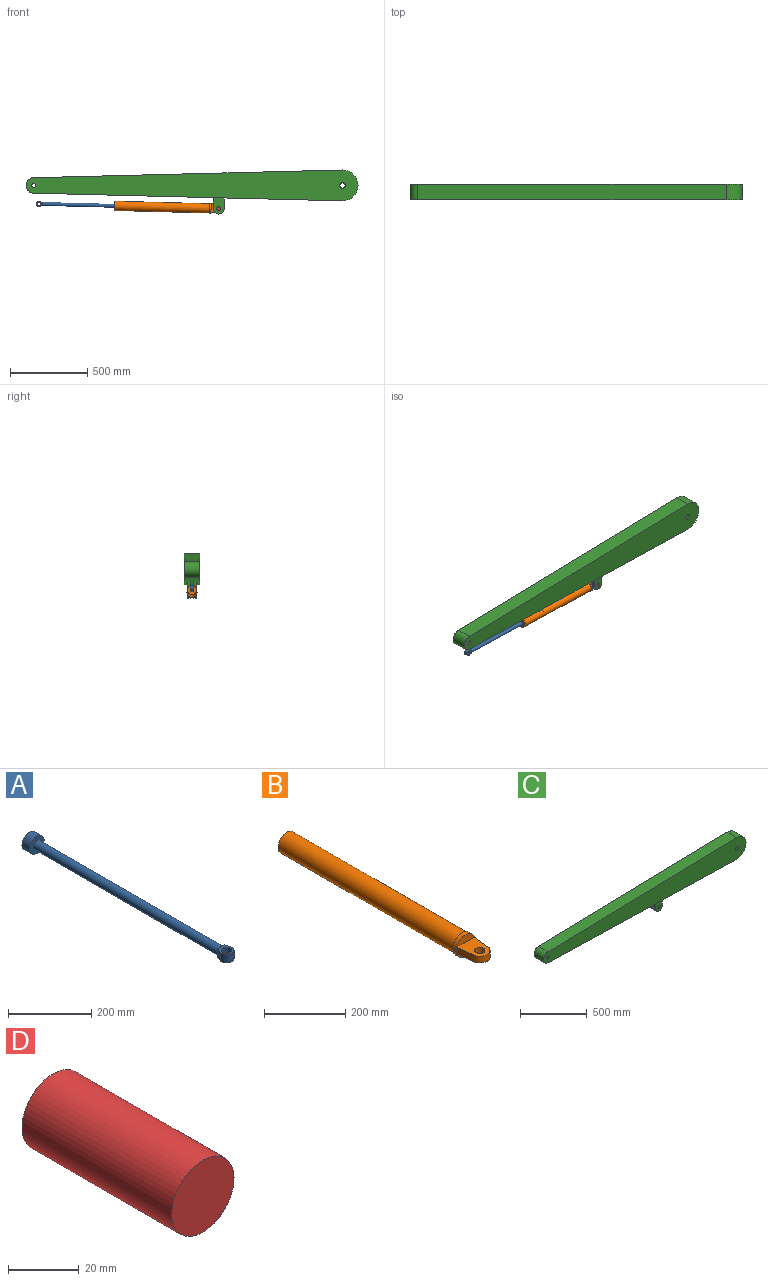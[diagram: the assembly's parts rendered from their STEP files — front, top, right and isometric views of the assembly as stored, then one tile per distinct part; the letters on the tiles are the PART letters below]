
ASSEMBLY  parts=4 mates=3
PART A: 14 faces, bbox 50x687.5x50 mm
  f0: plane 6.82x0.48mm, normal (0,-1,0), area 2.2mm2, adj f1,f8
  f1: cylinder r=12.47mm len=625mm, axis (0,1,0), area 48989.2mm2, adj f0,f2,f5,f6,f7
  f2: plane 6.82x0.48mm, normal (0,-1,0), area 2.2mm2, adj f1,f9
  f3: cylinder r=24.98mm len=49.95mm, axis (0,-1,0), area 3923.1mm2, adj f4,f5
  f4: plane 49.95x49.95mm, normal (0,1,0), area 1959.6mm2, adj f3
  f5: plane 49.95x49.95mm, normal (0,-1,0), area 1470.7mm2, adj f1,f3
  f6: plane 24x9.09mm, normal (0,1,0), area 57.7mm2, adj f1,f8,f9,f12
  f7: plane 24x9.09mm, normal (0,1,0), area 57.7mm2, adj f1,f8,f9,f13
  f8: plane 25x14.69mm, normal (0.95,0.3,0), area 385.5mm2, adj f0,f6,f7,f10,f12,f13
  f9: plane 25x14.69mm, normal (-0.95,0.3,0), area 385.5mm2, adj f2,f6,f7,f10,f12,f13
  f10: cylinder r=17.5mm len=35mm, axis (0,0,-1), area 1644mm2, adj f8,f9,f12,f13
  f11: cylinder r=12.47mm len=25mm, axis (0,0,-1), area 1959.6mm2, adj f12,f13
  f12: plane 37.5x35mm, normal (0,0,1), area 596.3mm2, adj f6,f8,f9,f10,f11
  f13: plane 37.5x35mm, normal (0,0,-1), area 596.3mm2, adj f7,f8,f9,f10,f11
PART B: 15 faces, bbox 65x699x65 mm
  f0: plane 65x65mm, normal (0,-1,0), area 2118.3mm2, adj f7,f10,f12,f13,f14
  f1: cylinder r=25mm len=600mm, axis (0,1,0), area 94247.8mm2, adj f3,f8
  f2: cylinder r=30mm len=612mm, axis (0,1,0), area 115359.3mm2, adj f5,f6
  f3: plane 50x50mm, normal (0,-1,0), area 1472.6mm2, adj f1,f4
  f4: cylinder r=12.5mm len=25mm, axis (0,-1,0), area 942.5mm2, adj f3,f5
  f5: plane 60x60mm, normal (0,1,0), area 2336.6mm2, adj f2,f4
  f6: plane 65x65mm, normal (0,1,0), area 490.9mm2, adj f2,f7
  f7: cylinder r=32.5mm len=65mm, axis (0,1,0), area 2450.4mm2, adj f0,f6
  f8: plane 50x50mm, normal (0,1,0), area 1963.5mm2, adj f1
  f9: cylinder r=25mm len=49.76mm, axis (0,0,-1), area 1473.5mm2, adj f10,f12,f13,f14
  f10: plane 52.43x20mm, normal (1,-0.1,0), area 1053.6mm2, adj f0,f9,f13,f14
  f11: cylinder r=12.5mm len=25mm, axis (0,0,-1), area 1570.8mm2, adj f13,f14
  f12: plane 52.43x20mm, normal (-1,-0.1,0), area 1053.6mm2, adj f0,f9,f13,f14
  f13: plane 75x60mm, normal (0,0,1), area 3247mm2, adj f0,f9,f10,f11,f12
  f14: plane 75x60mm, normal (0,0,-1), area 3247mm2, adj f0,f9,f10,f11,f12
PART C: 20 faces, bbox 2150x100x285 mm
  f0: cylinder r=50mm len=100mm, axis (0,1,0), area 15583mm2, adj f1,f3,f6,f7
  f1: plane 1998.75x100mm, normal (-0.03,0,-1), area 197837.5mm2, adj f0,f2,f6,f7,f8,f9,f10,f12
  f2: cylinder r=100mm len=200mm, axis (0,1,0), area 31916.1mm2, adj f1,f3,f6,f7
  f3: plane 1997.5x100mm, normal (-0.03,0,1), area 199812.4mm2, adj f0,f2,f6,f7
  f4: cylinder r=12.5mm len=100mm, axis (0,1,0), area 7854mm2, adj f6,f7
  f5: cylinder r=17.5mm len=100mm, axis (0,1,0), area 10995.6mm2, adj f6,f7
  f6: plane 2150x200mm, normal (0,-1,0), area 318260.1mm2, adj f0,f1,f2,f3,f4,f5
  f7: plane 2150x200mm, normal (0,1,0), area 318260.1mm2, adj f0,f1,f2,f3,f4,f5
  f8: plane 105.88x71.74mm, normal (0,-1,0), area 6334.9mm2, adj f1,f10,f11,f12,f13
  f9: plane 105.88x71.74mm, normal (0,1,0), area 6334.9mm2, adj f1,f10,f11,f12,f13
  f10: plane 70x15mm, normal (-1,0,0.03), area 1050.3mm2, adj f1,f8,f9,f11
  f11: cylinder r=35mm len=69.99mm, axis (0,1,0), area 1649.3mm2, adj f8,f9,f10,f12
  f12: plane 70x15mm, normal (1,0,-0.03), area 1050.3mm2, adj f1,f8,f9,f11
  f13: cylinder r=12.5mm len=25mm, axis (0,1,0), area 1178.1mm2, adj f8,f9
  f14: plane 105.88x71.74mm, normal (0,1,0), area 6334.9mm2, adj f1,f16,f17,f18,f19
  f15: plane 105.88x71.74mm, normal (0,-1,0), area 6334.9mm2, adj f1,f16,f17,f18,f19
  f16: plane 70x15mm, normal (-1,0,0.03), area 1050.3mm2, adj f1,f14,f15,f17
  f17: cylinder r=35mm len=69.99mm, axis (0,-1,0), area 1649.3mm2, adj f14,f15,f16,f18
  f18: plane 70x15mm, normal (1,0,-0.03), area 1050.3mm2, adj f1,f14,f15,f17
  f19: cylinder r=12.5mm len=25mm, axis (0,-1,0), area 1178.1mm2, adj f14,f15
PART D: 3 faces, bbox 25x60x25 mm
  f0: cylinder r=12.5mm len=60mm, axis (0,1,0), area 4712.4mm2, adj f1,f2
  f1: plane 25x25mm, normal (0,-1,0), area 490.9mm2, adj f0
  f2: plane 25x25mm, normal (0,1,0), area 490.9mm2, adj f0
PLACE A rot(axis=(0.57,0.58,-0.58),120.9deg) t=(-352.72,-860.35,-54.73)mm
PLACE B rot(axis=(0.59,-0.57,0.57),119.1deg) t=(-494.6,-860.35,-50.98)mm
PLACE C t=(-1031.08,-860.35,81.57)mm fixed
PLACE D t=(167.17,-830.35,-68.46)mm
MATE slider A.f3 <-> B.f2  axis (-1,0,0.03) through (-340.22,-860.35,-55.06)mm
MATE fastened D.f0 <-> C.f11  axis (0,1,0) through (167.17,-860.35,-68.46)mm
MATE revolute D.f0 <-> B.f11  axis (0,1,0) through (167.17,-860.35,-68.46)mm
